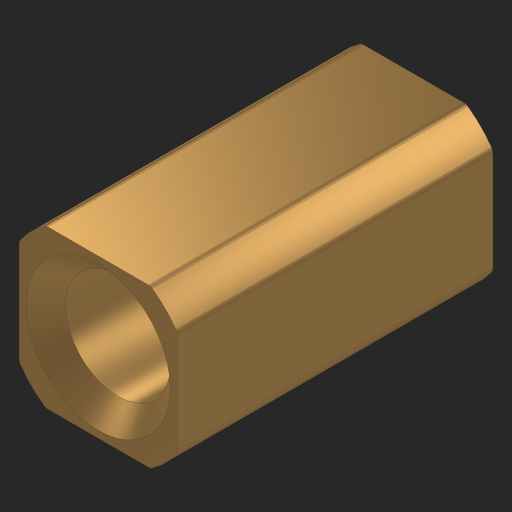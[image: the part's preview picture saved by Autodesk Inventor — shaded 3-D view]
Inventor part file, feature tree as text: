
AUTODESK INVENTOR PART (.ipt)
format: ipt  version: 2023 (Build 270158000, 158)  size: 165,376 bytes
history: native  units: in
note: dims shown in document units (in); Inventor stores cm internally (conversion verified against a paired STEP export)
features: extrude x2, sketch x2, fillet x1, chamfer x1
ambient origin geometry x8: Origin, YZ Plane, XZ Plane, XY Plane, X Axis, Y Axis, Z Axis, Center Point
bodies: Solid1 (feature_tree)
feature tree (6):
  extrude  "Extrusion1"  Depth=0.25in
  extrude  "Extrusion2"  Depth=0.01in
  fillet  "Fillet1"  Radius=0.5in
  chamfer  "Chamfer1"  Distance=0.01in
  sketch  "Sketch1"  dims[d0=0.3in d1=0.25in]
  sketch  "Sketch2"  dims[d2=0.5in d3=0.0in d4=0.166in d5=0.5in d6=0.0in d7=0.01in d8=0.0312in d9=0.125in d10=45.0deg]
